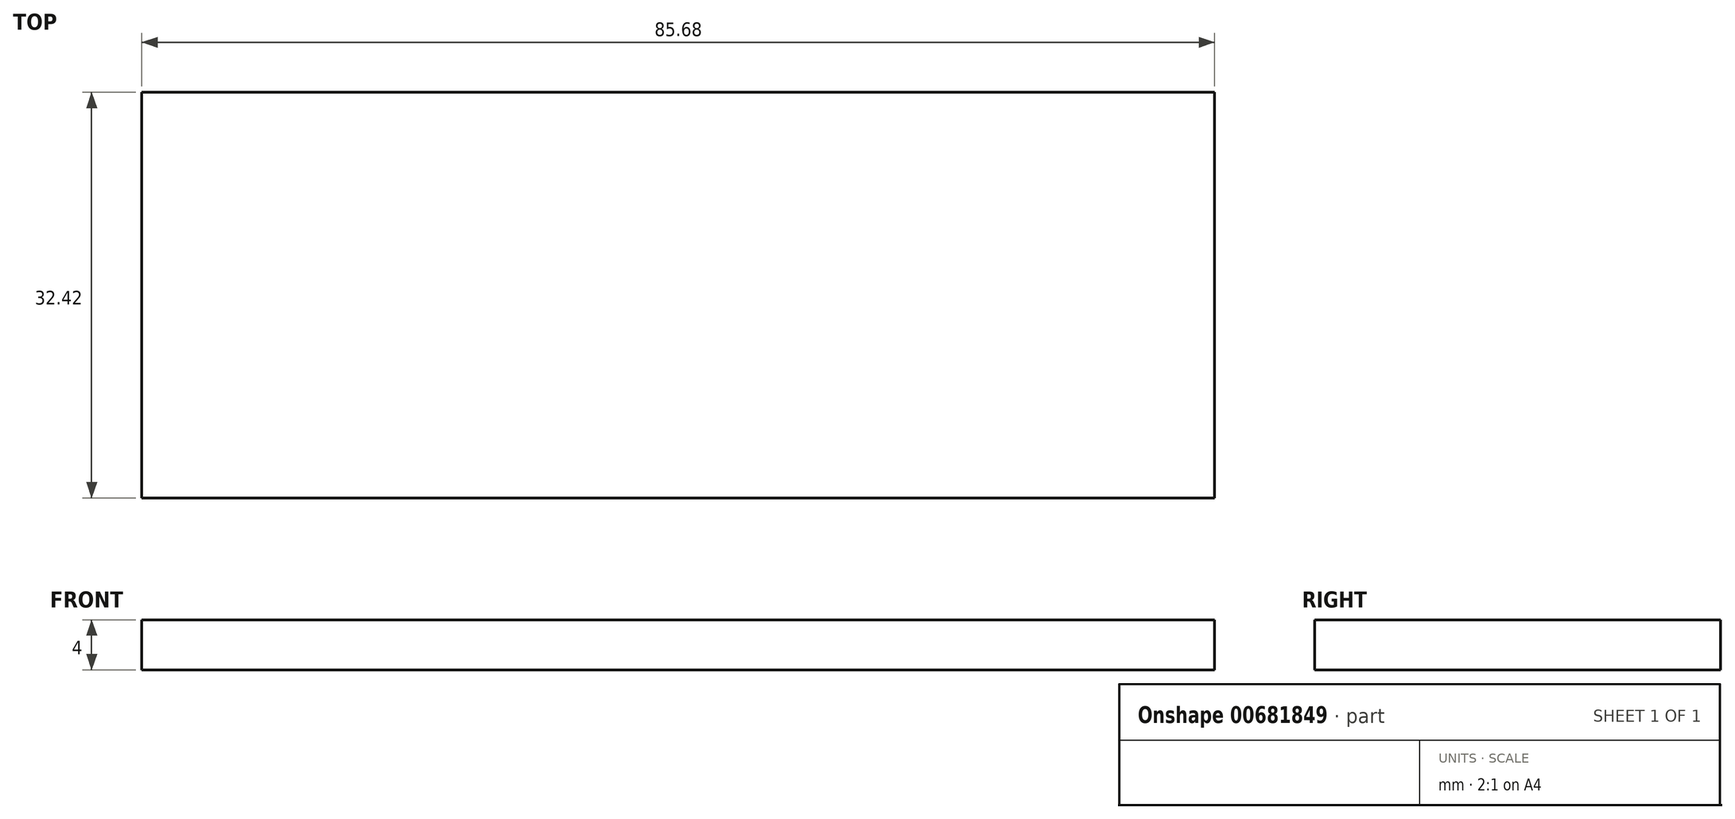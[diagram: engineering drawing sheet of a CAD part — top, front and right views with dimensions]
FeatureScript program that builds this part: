
annotation { "Feature Type Name" : "Feature", "Feature Type Description" : "" }
export const myFeature = defineFeature(function(context is Context, id is Id, definition is map)
    precondition{}
    {
        {
            var Q0;
            Q0=qCreatedBy(makeId("Top.planeOp"),FACE);
            var sketch = newSketch(context, id + "F0", { "sketchPlane" : qUnion([Q0])});
            skLineSegment(sketch, "E0.bottom", {"start": v(0, 0) * mm, "end": v(85.68, 0) * mm});
            skLineSegment(sketch, "E0.top", {"start": v(0, -32.42) * mm, "end": v(85.68, -32.42) * mm});
            skLineSegment(sketch, "E0.left", {"start": v(0, 0) * mm, "end": v(0, -32.42) * mm});
            skLineSegment(sketch, "E0.right", {"start": v(85.68, 0) * mm, "end": v(85.68, -32.42) * mm});
            skSolve(sketch);
        }
        {
            var Q0;
            Q0 = qSketchRegion(id + "F0", true);
            extrude(context, id + "F1", {"entities" : qUnion([Q0]), "depth" : 4 * mm, "offsetDistance" : 25.4 * mm});
        }
    });
